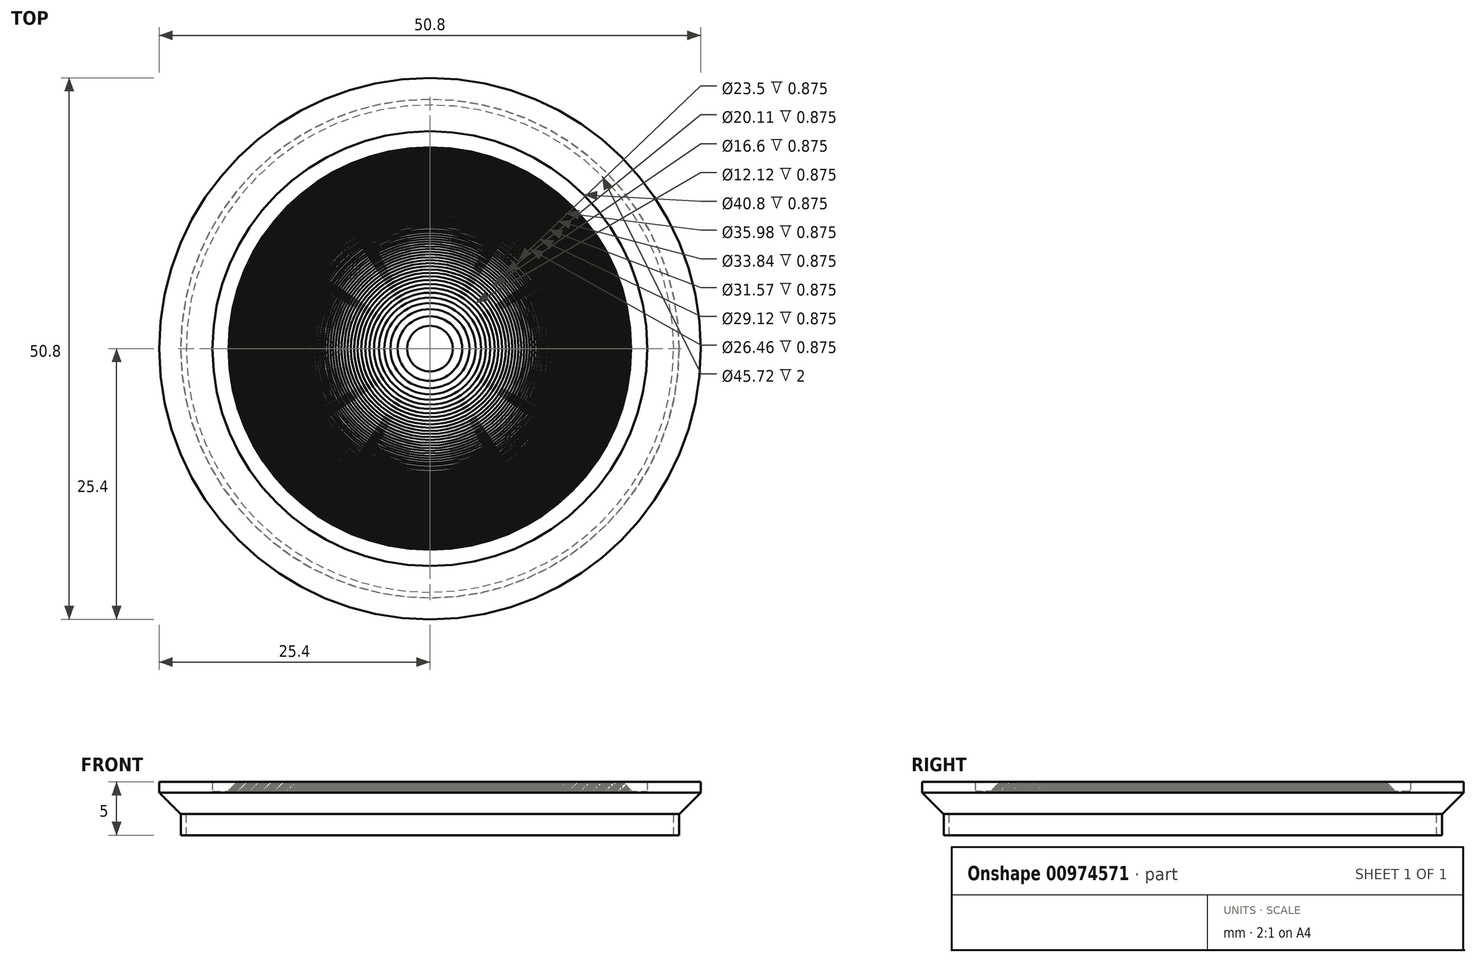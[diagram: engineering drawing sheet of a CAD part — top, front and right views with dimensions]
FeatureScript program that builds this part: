
annotation { "Feature Type Name" : "Feature", "Feature Type Description" : "" }
export const myFeature = defineFeature(function(context is Context, id is Id, definition is map)
    precondition{}
    {
        {
            var Q0;
            Q0=qCreatedBy(makeId("Front.planeOp"),FACE);
            var sketch = newSketch(context, id + "F0", { "sketchPlane" : qUnion([Q0])});
            skLineSegment(sketch, "E0", {"start": v(-10.56, 1.5) * mm, "end": v(-12.7, 1.5) * mm});
            skLineSegment(sketch, "E1", {"start": v(-10.56, 1.37) * mm, "end": v(-10.56, 1.5) * mm});
            skLineSegment(sketch, "E2", {"start": v(-9.67, 1.25) * mm, "end": v(-9.67, 1.37) * mm});
            skLineSegment(sketch, "E3", {"start": v(-9.67, 1.37) * mm, "end": v(-10.56, 1.37) * mm});
            skLineSegment(sketch, "E4", {"start": v(-8.99, 1.12) * mm, "end": v(-8.99, 1.25) * mm});
            skLineSegment(sketch, "E5", {"start": v(-8.99, 1.25) * mm, "end": v(-9.67, 1.25) * mm});
            skLineSegment(sketch, "E6", {"start": v(-8.42, 1) * mm, "end": v(-8.42, 1.12) * mm});
            skLineSegment(sketch, "E7", {"start": v(-8.42, 1.12) * mm, "end": v(-8.99, 1.12) * mm});
            skLineSegment(sketch, "E8", {"start": v(-7.9, 0.87) * mm, "end": v(-7.9, 1) * mm});
            skLineSegment(sketch, "E9", {"start": v(-7.9, 1) * mm, "end": v(-8.42, 1) * mm});
            skLineSegment(sketch, "E10", {"start": v(-7.45, 0.75) * mm, "end": v(-7.45, 0.87) * mm});
            skLineSegment(sketch, "E11", {"start": v(-7.45, 0.87) * mm, "end": v(-7.9, 0.87) * mm});
            skLineSegment(sketch, "E12", {"start": v(-7.03, 0.62) * mm, "end": v(-7.03, 0.75) * mm});
            skLineSegment(sketch, "E13", {"start": v(-7.03, 0.75) * mm, "end": v(-7.45, 0.75) * mm});
            skLineSegment(sketch, "E14", {"start": v(-6.64, 0.62) * mm, "end": v(-7.03, 0.62) * mm});
            skLineSegment(sketch, "E15", {"start": v(-6.27, 1.37) * mm, "end": v(-6.27, 1.5) * mm});
            skLineSegment(sketch, "E16", {"start": v(-6.64, 0.62) * mm, "end": v(-6.64, 1.5) * mm});
            skLineSegment(sketch, "E17", {"start": v(-6.64, 1.5) * mm, "end": v(-6.27, 1.5) * mm});
            skLineSegment(sketch, "E18", {"start": v(-5.92, 1.25) * mm, "end": v(-5.92, 1.37) * mm});
            skLineSegment(sketch, "E19", {"start": v(-5.92, 1.37) * mm, "end": v(-6.27, 1.37) * mm});
            skLineSegment(sketch, "E20", {"start": v(-5.6, 1.12) * mm, "end": v(-5.6, 1.25) * mm});
            skLineSegment(sketch, "E21", {"start": v(-5.6, 1.25) * mm, "end": v(-5.92, 1.25) * mm});
            skLineSegment(sketch, "E22", {"start": v(-5.28, 1) * mm, "end": v(-5.28, 1.12) * mm});
            skLineSegment(sketch, "E23", {"start": v(-5.28, 1.12) * mm, "end": v(-5.6, 1.12) * mm});
            skLineSegment(sketch, "E24", {"start": v(-4.97, 0.87) * mm, "end": v(-4.97, 1) * mm});
            skLineSegment(sketch, "E25", {"start": v(-4.97, 1) * mm, "end": v(-5.28, 1) * mm});
            skLineSegment(sketch, "E26", {"start": v(-4.68, 0.62) * mm, "end": v(-4.68, 0.87) * mm});
            skLineSegment(sketch, "E27", {"start": v(-4.68, 0.87) * mm, "end": v(-4.97, 0.87) * mm});
            skLineSegment(sketch, "E28", {"start": v(-4.4, 0.62) * mm, "end": v(-4.68, 0.62) * mm});
            skLineSegment(sketch, "E29", {"start": v(-4.4, 0.62) * mm, "end": v(-4.4, 1.5) * mm});
            skLineSegment(sketch, "E30", {"start": v(-4.13, 1.37) * mm, "end": v(-4.13, 1.5) * mm});
            skLineSegment(sketch, "E31", {"start": v(-4.13, 1.5) * mm, "end": v(-4.4, 1.5) * mm});
            skLineSegment(sketch, "E32", {"start": v(-3.86, 1.25) * mm, "end": v(-3.86, 1.37) * mm});
            skLineSegment(sketch, "E33", {"start": v(-3.86, 1.37) * mm, "end": v(-4.13, 1.37) * mm});
            skLineSegment(sketch, "E34", {"start": v(-3.6, 1.12) * mm, "end": v(-3.6, 1.25) * mm});
            skLineSegment(sketch, "E35", {"start": v(-3.6, 1.25) * mm, "end": v(-3.86, 1.25) * mm});
            skLineSegment(sketch, "E36", {"start": v(-3.35, 1) * mm, "end": v(-3.35, 1.12) * mm});
            skLineSegment(sketch, "E37", {"start": v(-3.35, 1.12) * mm, "end": v(-3.6, 1.12) * mm});
            skLineSegment(sketch, "E38", {"start": v(-3.11, 0.87) * mm, "end": v(-3.11, 1) * mm});
            skLineSegment(sketch, "E39", {"start": v(-3.11, 1) * mm, "end": v(-3.35, 1) * mm});
            skLineSegment(sketch, "E40", {"start": v(-2.88, 0.62) * mm, "end": v(-2.88, 0.87) * mm});
            skLineSegment(sketch, "E41", {"start": v(-2.88, 0.87) * mm, "end": v(-3.11, 0.87) * mm});
            skLineSegment(sketch, "E42", {"start": v(-2.64, 0.62) * mm, "end": v(-2.88, 0.62) * mm});
            skLineSegment(sketch, "E43", {"start": v(-2.42, 1.37) * mm, "end": v(-2.42, 1.5) * mm});
            skLineSegment(sketch, "E44", {"start": v(-2.64, 0.62) * mm, "end": v(-2.64, 1.5) * mm});
            skLineSegment(sketch, "E45", {"start": v(-2.64, 1.5) * mm, "end": v(-2.42, 1.5) * mm});
            skLineSegment(sketch, "E46", {"start": v(-2.2, 1.25) * mm, "end": v(-2.2, 1.37) * mm});
            skLineSegment(sketch, "E47", {"start": v(-2.2, 1.37) * mm, "end": v(-2.42, 1.37) * mm});
            skLineSegment(sketch, "E48", {"start": v(-1.98, 1.12) * mm, "end": v(-1.98, 1.25) * mm});
            skLineSegment(sketch, "E49", {"start": v(-1.98, 1.25) * mm, "end": v(-2.2, 1.25) * mm});
            skLineSegment(sketch, "E50", {"start": v(-1.76, 1) * mm, "end": v(-1.76, 1.12) * mm});
            skLineSegment(sketch, "E51", {"start": v(-1.76, 1.12) * mm, "end": v(-1.98, 1.12) * mm});
            skLineSegment(sketch, "E52", {"start": v(-1.55, 0.87) * mm, "end": v(-1.55, 1) * mm});
            skLineSegment(sketch, "E53", {"start": v(-1.55, 1) * mm, "end": v(-1.76, 1) * mm});
            skLineSegment(sketch, "E54", {"start": v(-1.35, 0.75) * mm, "end": v(-1.35, 0.87) * mm});
            skLineSegment(sketch, "E55", {"start": v(-1.35, 0.87) * mm, "end": v(-1.55, 0.87) * mm});
            skLineSegment(sketch, "E56", {"start": v(-1.15, 0.62) * mm, "end": v(-1.15, 0.75) * mm});
            skLineSegment(sketch, "E57", {"start": v(-1.15, 0.75) * mm, "end": v(-1.35, 0.75) * mm});
            skLineSegment(sketch, "E58", {"start": v(-0.95, 0.62) * mm, "end": v(-1.15, 0.62) * mm});
            skLineSegment(sketch, "E59", {"start": v(-0.76, 1.37) * mm, "end": v(-0.76, 1.5) * mm});
            skLineSegment(sketch, "E60", {"start": v(-0.95, 0.62) * mm, "end": v(-0.95, 1.5) * mm});
            skLineSegment(sketch, "E61", {"start": v(-0.95, 1.5) * mm, "end": v(-0.76, 1.5) * mm});
            skLineSegment(sketch, "E62", {"start": v(-0.56, 1.25) * mm, "end": v(-0.56, 1.37) * mm});
            skLineSegment(sketch, "E63", {"start": v(-0.56, 1.37) * mm, "end": v(-0.76, 1.37) * mm});
            skLineSegment(sketch, "E64", {"start": v(-0.38, 1.12) * mm, "end": v(-0.38, 1.25) * mm});
            skLineSegment(sketch, "E65", {"start": v(-0.38, 1.25) * mm, "end": v(-0.56, 1.25) * mm});
            skLineSegment(sketch, "E66", {"start": v(-0.19, 1) * mm, "end": v(-0.19, 1.12) * mm});
            skLineSegment(sketch, "E67", {"start": v(-0.19, 1.12) * mm, "end": v(-0.38, 1.12) * mm});
            skLineSegment(sketch, "E68", {"start": v(0, 0.87) * mm, "end": v(0, 1) * mm});
            skLineSegment(sketch, "E69", {"start": v(0, 1) * mm, "end": v(-0.19, 1) * mm});
            skLineSegment(sketch, "E70", {"start": v(0.18, 0.75) * mm, "end": v(0.18, 0.87) * mm});
            skLineSegment(sketch, "E71", {"start": v(0.18, 0.87) * mm, "end": v(0, 0.87) * mm});
            skLineSegment(sketch, "E72", {"start": v(0.35, 0.62) * mm, "end": v(0.35, 0.75) * mm});
            skLineSegment(sketch, "E73", {"start": v(0.35, 0.75) * mm, "end": v(0.18, 0.75) * mm});
            skLineSegment(sketch, "E74", {"start": v(0.53, 0.62) * mm, "end": v(0.35, 0.62) * mm});
            skLineSegment(sketch, "E75", {"start": v(0.53, 0.62) * mm, "end": v(0.53, 1.5) * mm});
            skLineSegment(sketch, "E76", {"start": v(0.7, 1.37) * mm, "end": v(0.7, 1.5) * mm});
            skLineSegment(sketch, "E77", {"start": v(0.7, 1.5) * mm, "end": v(0.53, 1.5) * mm});
            skLineSegment(sketch, "E78", {"start": v(0.88, 1.25) * mm, "end": v(0.88, 1.37) * mm});
            skLineSegment(sketch, "E79", {"start": v(0.88, 1.37) * mm, "end": v(0.7, 1.37) * mm});
            skLineSegment(sketch, "E80", {"start": v(1.04, 1.12) * mm, "end": v(1.04, 1.25) * mm});
            skLineSegment(sketch, "E81", {"start": v(1.04, 1.25) * mm, "end": v(0.88, 1.25) * mm});
            skLineSegment(sketch, "E82", {"start": v(1.21, 1) * mm, "end": v(1.21, 1.12) * mm});
            skLineSegment(sketch, "E83", {"start": v(1.21, 1.12) * mm, "end": v(1.04, 1.12) * mm});
            skLineSegment(sketch, "E84", {"start": v(1.38, 0.87) * mm, "end": v(1.38, 1) * mm});
            skLineSegment(sketch, "E85", {"start": v(1.38, 1) * mm, "end": v(1.21, 1) * mm});
            skLineSegment(sketch, "E86", {"start": v(1.54, 0.75) * mm, "end": v(1.54, 0.87) * mm});
            skLineSegment(sketch, "E87", {"start": v(1.54, 0.87) * mm, "end": v(1.38, 0.87) * mm});
            skLineSegment(sketch, "E88", {"start": v(1.7, 0.62) * mm, "end": v(1.7, 0.75) * mm});
            skLineSegment(sketch, "E89", {"start": v(1.7, 0.75) * mm, "end": v(1.54, 0.75) * mm});
            skLineSegment(sketch, "E90", {"start": v(1.86, 0.62) * mm, "end": v(1.7, 0.62) * mm});
            skLineSegment(sketch, "E91", {"start": v(2.02, 1.37) * mm, "end": v(2.02, 1.5) * mm});
            skLineSegment(sketch, "E92", {"start": v(1.86, 0.62) * mm, "end": v(1.86, 1.5) * mm});
            skLineSegment(sketch, "E93", {"start": v(1.86, 1.5) * mm, "end": v(2.02, 1.5) * mm});
            skLineSegment(sketch, "E94", {"start": v(2.18, 1.25) * mm, "end": v(2.18, 1.37) * mm});
            skLineSegment(sketch, "E95", {"start": v(2.18, 1.37) * mm, "end": v(2.02, 1.37) * mm});
            skLineSegment(sketch, "E96", {"start": v(2.33, 1.12) * mm, "end": v(2.33, 1.25) * mm});
            skLineSegment(sketch, "E97", {"start": v(2.33, 1.25) * mm, "end": v(2.18, 1.25) * mm});
            skLineSegment(sketch, "E98", {"start": v(2.49, 1) * mm, "end": v(2.49, 1.12) * mm});
            skLineSegment(sketch, "E99", {"start": v(2.49, 1.12) * mm, "end": v(2.33, 1.12) * mm});
            skLineSegment(sketch, "E100", {"start": v(2.64, 0.87) * mm, "end": v(2.64, 1) * mm});
            skLineSegment(sketch, "E101", {"start": v(2.64, 1) * mm, "end": v(2.49, 1) * mm});
            skLineSegment(sketch, "E102", {"start": v(2.79, 0.75) * mm, "end": v(2.79, 0.87) * mm});
            skLineSegment(sketch, "E103", {"start": v(2.79, 0.87) * mm, "end": v(2.64, 0.87) * mm});
            skLineSegment(sketch, "E104", {"start": v(2.94, 0.62) * mm, "end": v(2.94, 0.75) * mm});
            skLineSegment(sketch, "E105", {"start": v(2.94, 0.75) * mm, "end": v(2.79, 0.75) * mm});
            skLineSegment(sketch, "E106", {"start": v(3.08, 0.62) * mm, "end": v(2.94, 0.62) * mm});
            skLineSegment(sketch, "E107", {"start": v(3.08, 0.62) * mm, "end": v(3.08, 1.5) * mm});
            skLineSegment(sketch, "E108", {"start": v(3.23, 1.37) * mm, "end": v(3.23, 1.5) * mm});
            skLineSegment(sketch, "E109", {"start": v(3.23, 1.5) * mm, "end": v(3.08, 1.5) * mm});
            skLineSegment(sketch, "E110", {"start": v(3.38, 1.25) * mm, "end": v(3.38, 1.37) * mm});
            skLineSegment(sketch, "E111", {"start": v(3.38, 1.37) * mm, "end": v(3.23, 1.37) * mm});
            skLineSegment(sketch, "E112", {"start": v(3.52, 1.12) * mm, "end": v(3.52, 1.25) * mm});
            skLineSegment(sketch, "E113", {"start": v(3.52, 1.25) * mm, "end": v(3.38, 1.25) * mm});
            skLineSegment(sketch, "E114", {"start": v(3.66, 1) * mm, "end": v(3.66, 1.12) * mm});
            skLineSegment(sketch, "E115", {"start": v(3.66, 1.12) * mm, "end": v(3.52, 1.12) * mm});
            skLineSegment(sketch, "E116", {"start": v(3.8, 0.87) * mm, "end": v(3.8, 1) * mm});
            skLineSegment(sketch, "E117", {"start": v(3.8, 1) * mm, "end": v(3.66, 1) * mm});
            skLineSegment(sketch, "E118", {"start": v(3.95, 0.75) * mm, "end": v(3.95, 0.87) * mm});
            skLineSegment(sketch, "E119", {"start": v(3.95, 0.87) * mm, "end": v(3.8, 0.87) * mm});
            skLineSegment(sketch, "E120", {"start": v(4.08, 0.62) * mm, "end": v(4.08, 0.75) * mm});
            skLineSegment(sketch, "E121", {"start": v(4.08, 0.75) * mm, "end": v(3.95, 0.75) * mm});
            skLineSegment(sketch, "E122", {"start": v(4.22, 0.62) * mm, "end": v(4.08, 0.62) * mm});
            skLineSegment(sketch, "E123", {"start": v(4.22, 0.62) * mm, "end": v(4.22, 1.5) * mm});
            skLineSegment(sketch, "E124", {"start": v(4.36, 1.37) * mm, "end": v(4.36, 1.5) * mm});
            skLineSegment(sketch, "E125", {"start": v(4.36, 1.5) * mm, "end": v(4.22, 1.5) * mm});
            skLineSegment(sketch, "E126", {"start": v(4.5, 1.25) * mm, "end": v(4.5, 1.37) * mm});
            skLineSegment(sketch, "E127", {"start": v(4.5, 1.37) * mm, "end": v(4.36, 1.37) * mm});
            skLineSegment(sketch, "E128", {"start": v(4.63, 1.12) * mm, "end": v(4.63, 1.25) * mm});
            skLineSegment(sketch, "E129", {"start": v(4.63, 1.25) * mm, "end": v(4.5, 1.25) * mm});
            skLineSegment(sketch, "E130", {"start": v(4.76, 1) * mm, "end": v(4.76, 1.12) * mm});
            skLineSegment(sketch, "E131", {"start": v(4.76, 1.12) * mm, "end": v(4.63, 1.12) * mm});
            skLineSegment(sketch, "E132", {"start": v(4.9, 0.87) * mm, "end": v(4.9, 1) * mm});
            skLineSegment(sketch, "E133", {"start": v(4.9, 1) * mm, "end": v(4.76, 1) * mm});
            skLineSegment(sketch, "E134", {"start": v(5.03, 0.75) * mm, "end": v(5.03, 0.87) * mm});
            skLineSegment(sketch, "E135", {"start": v(5.03, 0.87) * mm, "end": v(4.9, 0.87) * mm});
            skLineSegment(sketch, "E136", {"start": v(5.16, 0.62) * mm, "end": v(5.16, 0.75) * mm});
            skLineSegment(sketch, "E137", {"start": v(5.16, 0.75) * mm, "end": v(5.03, 0.75) * mm});
            skLineSegment(sketch, "E138", {"start": v(5.29, 0.62) * mm, "end": v(5.16, 0.62) * mm});
            skLineSegment(sketch, "E139", {"start": v(5.29, 0.62) * mm, "end": v(5.29, 1.5) * mm});
            skLineSegment(sketch, "E140", {"start": v(5.42, 1.37) * mm, "end": v(5.42, 1.5) * mm});
            skLineSegment(sketch, "E141", {"start": v(5.42, 1.5) * mm, "end": v(5.29, 1.5) * mm});
            skLineSegment(sketch, "E142", {"start": v(5.55, 1.25) * mm, "end": v(5.55, 1.37) * mm});
            skLineSegment(sketch, "E143", {"start": v(5.55, 1.37) * mm, "end": v(5.42, 1.37) * mm});
            skLineSegment(sketch, "E144", {"start": v(5.67, 1.12) * mm, "end": v(5.67, 1.25) * mm});
            skLineSegment(sketch, "E145", {"start": v(5.67, 1.25) * mm, "end": v(5.55, 1.25) * mm});
            skLineSegment(sketch, "E146", {"start": v(5.8, 1) * mm, "end": v(5.8, 1.12) * mm});
            skLineSegment(sketch, "E147", {"start": v(5.8, 1.12) * mm, "end": v(5.67, 1.12) * mm});
            skLineSegment(sketch, "E148", {"start": v(5.93, 0.87) * mm, "end": v(5.93, 1) * mm});
            skLineSegment(sketch, "E149", {"start": v(5.93, 1) * mm, "end": v(5.8, 1) * mm});
            skLineSegment(sketch, "E150", {"start": v(6.05, 0.75) * mm, "end": v(6.05, 0.87) * mm});
            skLineSegment(sketch, "E151", {"start": v(6.05, 0.87) * mm, "end": v(5.93, 0.87) * mm});
            skLineSegment(sketch, "E152", {"start": v(6.17, 0.62) * mm, "end": v(6.17, 0.75) * mm});
            skLineSegment(sketch, "E153", {"start": v(6.17, 0.75) * mm, "end": v(6.05, 0.75) * mm});
            skLineSegment(sketch, "E154", {"start": v(12.7, -1.5) * mm, "end": v(12.7, 1.5) * mm});
            skLineSegment(sketch, "E155", {"start": v(12.7, 1.5) * mm, "end": v(7.7, 1.5) * mm});
            skLineSegment(sketch, "E156", {"start": v(7.7, 1.5) * mm, "end": v(7.7, 0.62) * mm});
            skLineSegment(sketch, "E157", {"start": v(7.7, 0.62) * mm, "end": v(6.17, 0.62) * mm});
            skLineSegment(sketch, "E158", {"start": v(-12.7, -1.5) * mm, "end": v(12.7, -1.5) * mm});
            skLineSegment(sketch, "E159", {"start": v(-12.7, -1.5) * mm, "end": v(-12.7, 1.5) * mm});
            skSolve(sketch);
        }
        {
            var Q0;
            Q0=makeQuery(id+"F0.imprint","IMPRINT",FACE,{"disambiguationData":[TD([[makeQuery(id+"F0.imprint","IMPRINT",EDGE,{"derivedFrom":sQuery(id+"F0.wireOp",EDGE,"E0")}),1.0]])]});
            var Q1;
            Q1=sQuery(id+"F0.wireOp",EDGE,"E159");
            revolve(context, id + "F1", {"surfaceOperationType" : NewSurfaceOperationType.NEW, "entities" : qUnion([Q0]), "axis" : qUnion([Q1]), "revolveType" : RevolveType.FULL});
        }
        {
            var Q0;
            Q0=makeQuery(id+"F1.opRevolve","SWEPT_EDGE",EDGE,{"disambiguationData":[OSD([sQuery(id+"F0.wireOp",EDGE,"E154"),sQuery(id+"F0.wireOp",EDGE,"E158")])]});
            chamfer(context, id + "F2", {"entities" : qUnion([Q0]), "width" : 2 * mm, "tangentPropagation" : true});
        }
        {
            var Q0;
            Q0=makeQuery(id+"F1.opRevolve","SWEPT_FACE",FACE,{"disambiguationData":[OSD([sQuery(id+"F0.wireOp",EDGE,"E158")])]});
            var sketch = newSketch(context, id + "F3", { "sketchPlane" : qUnion([Q0])});
            skCircle(sketch, "E160", {"center": v(-12.7, 0) * mm, "radius": 23.37 * mm});
            skCircle(sketch, "E161", {"center": v(-12.7, 0) * mm, "radius": 22.86 * mm});
            skSolve(sketch);
        }
        {
            var Q0;
            Q0=makeQuery(id+"F3.imprint","IMPRINT",FACE,{"disambiguationData":[TD([[makeQuery(id+"F3.imprint","IMPRINT",EDGE,{"derivedFrom":sQuery(id+"F3.wireOp",EDGE,"E160")}),1.0]])]});
            extrude(context, id + "F4", {"entities" : qUnion([Q0]), "operationType" : NewBodyOperationType.ADD, "depth" : 2 * mm, "offsetDistance" : 25.4 * mm});
        }
    });
